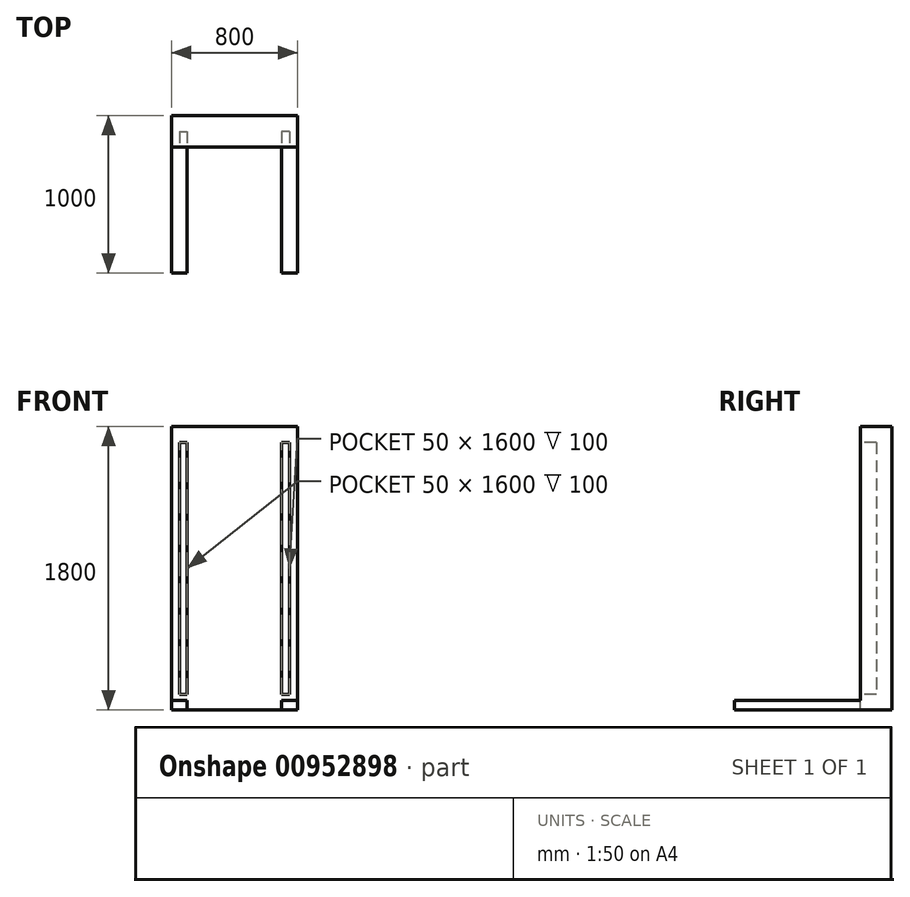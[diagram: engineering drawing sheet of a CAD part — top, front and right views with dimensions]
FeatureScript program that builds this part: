
annotation { "Feature Type Name" : "Feature", "Feature Type Description" : "" }
export const myFeature = defineFeature(function(context is Context, id is Id, definition is map)
    precondition{}
    {
        {
            var Q0;
            Q0=qCreatedBy(makeId("Front.planeOp"),FACE);
            var sketch = newSketch(context, id + "F0", { "sketchPlane" : qUnion([Q0])});
            skLineSegment(sketch, "E0", {"start": v(0, 0) * mm, "end": v(800, 0) * mm});
            skLineSegment(sketch, "E1", {"start": v(800, 0) * mm, "end": v(800, 1800) * mm});
            skLineSegment(sketch, "E2", {"start": v(800, 1800) * mm, "end": v(0, 1800) * mm});
            skLineSegment(sketch, "E3", {"start": v(0, 1800) * mm, "end": v(0, 0) * mm});
            skSolve(sketch);
        }
        {
            var Q0;
            Q0 = qSketchRegion(id + "F0", true);
            extrude(context, id + "F1", {"entities" : qUnion([Q0]), "depth" : 200 * mm, "offsetDistance" : 25 * mm});
        }
        {
            var Q0;
            Q0=makeQuery(id+"F1.opExtrude","SWEPT_FACE",FACE,{"disambiguationData":[OSD([sQuery(id+"F0.wireOp",EDGE,"E3")])]});
            cPlane(context, id + "F2", {"entities" : qUnion([Q0]), "cplaneType" : CPlaneType.OFFSET, "offset" : 400 * mm, "oppositeDirection" : true, "width" : 150 * mm, "height" : 150 * mm});
        }
        {
            var Q0;
            Q0=makeQuery(id+"F1.opExtrude","CAP_FACE",FACE,{"disambiguationData":[OSD([sQuery(id+"F0.wireOp",EDGE,"E0"),sQuery(id+"F0.wireOp",EDGE,"E1"),sQuery(id+"F0.wireOp",EDGE,"E2"),sQuery(id+"F0.wireOp",EDGE,"E3")])],"isStart":false});
            var sketch = newSketch(context, id + "F3", { "sketchPlane" : qUnion([Q0])});
            skLineSegment(sketch, "E4.bottom", {"start": v(50, 1700) * mm, "end": v(100, 1700) * mm});
            skLineSegment(sketch, "E4.top", {"start": v(50, 100) * mm, "end": v(100, 100) * mm});
            skLineSegment(sketch, "E4.left", {"start": v(50, 1700) * mm, "end": v(50, 100) * mm});
            skLineSegment(sketch, "E4.right", {"start": v(100, 1700) * mm, "end": v(100, 100) * mm});
            skLineSegment(sketch, "E5.MirrorCS", {"start": v(750, 1700) * mm, "end": v(750, 100) * mm});
            skLineSegment(sketch, "E6.MirrorCS", {"start": v(700, 1700) * mm, "end": v(700, 100) * mm});
            skLineSegment(sketch, "E7.MirrorCS", {"start": v(750, 1700) * mm, "end": v(700, 1700) * mm});
            skLineSegment(sketch, "E8.MirrorCS", {"start": v(750, 100) * mm, "end": v(700, 100) * mm});
            skSolve(sketch);
        }
        {
            var Q0;
            Q0=makeQuery(id+"F3.imprint","IMPRINT",FACE,{"disambiguationData":[TD([[makeQuery(id+"F3.imprint","IMPRINT",EDGE,{"derivedFrom":sQuery(id+"F3.wireOp",EDGE,"E4.bottom")}),-1.0]])]});
            var Q1;
            Q1=makeQuery(id+"F3.imprint","IMPRINT",FACE,{"disambiguationData":[TD([[makeQuery(id+"F3.imprint","IMPRINT",EDGE,{"derivedFrom":sQuery(id+"F3.wireOp",EDGE,"E5.MirrorCS")}),-1.0]])]});
            extrude(context, id + "F4", {"entities" : qUnion([Q0, Q1]), "operationType" : NewBodyOperationType.REMOVE, "oppositeDirection" : true, "depth" : 100 * mm, "offsetDistance" : 25 * mm});
        }
        {
            var Q0;
            Q0=makeQuery(id+"F1.opExtrude","CAP_FACE",FACE,{"disambiguationData":[OSD([sQuery(id+"F0.wireOp",EDGE,"E0"),sQuery(id+"F0.wireOp",EDGE,"E1"),sQuery(id+"F0.wireOp",EDGE,"E2"),sQuery(id+"F0.wireOp",EDGE,"E3")])],"isStart":false});
            var sketch = newSketch(context, id + "F5", { "sketchPlane" : qUnion([Q0])});
            skPoint(sketch, "E9.oppositeSnap0", {"position": v(725, 100) * mm});
            skLineSegment(sketch, "E9.bottom", {"start": v(800, 0) * mm, "end": v(700, 0) * mm});
            skLineSegment(sketch, "E9.top", {"start": v(800, 60) * mm, "end": v(700, 60) * mm});
            skLineSegment(sketch, "E9.left", {"start": v(800, 0) * mm, "end": v(800, 60) * mm});
            skLineSegment(sketch, "E9.right", {"start": v(700, 0) * mm, "end": v(700, 60) * mm});
            skLineSegment(sketch, "E10.MirrorCS", {"start": v(100, 0) * mm, "end": v(100, 60) * mm});
            skLineSegment(sketch, "E11.MirrorCS", {"start": v(0, 60) * mm, "end": v(100, 60) * mm});
            skLineSegment(sketch, "E12.MirrorCS", {"start": v(0, 0) * mm, "end": v(0, 60) * mm});
            skLineSegment(sketch, "E13.MirrorCS", {"start": v(0, 0) * mm, "end": v(100, 0) * mm});
            skSolve(sketch);
        }
        {
            var Q0;
            {var subQ3=sQuery(id+"F5.wireOp",EDGE,"E10.MirrorCS");Q0=makeQuery(id+"F5.imprint","IMPRINT",FACE,{"disambiguationData":[TD([[makeQuery(id+"F5.imprint","IMPRINT",EDGE,{"derivedFrom":subQ3}),1.0]])]});}
            var Q1;
            Q1=makeQuery(id+"F5.imprint","IMPRINT",FACE,{"disambiguationData":[TD([[makeQuery(id+"F5.imprint","IMPRINT",EDGE,{"derivedFrom":sQuery(id+"F5.wireOp",EDGE,"E9.bottom")}),1.0]])]});
            extrude(context, id + "F6", {"entities" : qUnion([Q0, Q1]), "operationType" : NewBodyOperationType.ADD, "depth" : 800 * mm, "offsetDistance" : 25 * mm});
        }
    });
